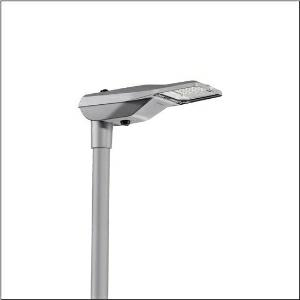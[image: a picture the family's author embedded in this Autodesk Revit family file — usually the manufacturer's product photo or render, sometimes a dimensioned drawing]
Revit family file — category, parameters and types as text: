
# Revit family: streetlight_sl_21_iq_micro___st1_0a_5xe1d31y08cb_1c09
name_source: partatom
category: Lighting Fixtures
units: mm (PartAtom-declared; Revit-internal decimal feet)

## family parameters
Cut with Voids When Loaded = No
Host = Face
Light Source = No
Part Type = Normal
Room Calculation Point = No
Round Connector Dimension = Use Diameter
Shared = No

## types (1)
- --- (1 x LED, 2880 lm, 19.1 W, 3000K)
    Apparent Load = 19 VA
    CIE Flux Codes = 37 72 97 100 100
    Color Rendering = 70
    Color Temperature = 3000K
    Default Elevation = 1800 mm
    Description = Streetlight SL 21 iQ micro, mast luminaire, primary light control with lens, of PMMA, primary optical cover: cover, of toughened safety glass, transparent, light distribution: ST1.0a, light emission: direct distribution, primary light characteristic: asymmetric, installation type: post-top, side-entry, LED, High Power LED, rated luminous flux: 2.880lm, luminous efficacy: 151lm/W, light colour: 730, colour temperature: 3000K, control gear: iQ-Street Remote, D4i with power reduction, control: pre-setting: logarithmic dimming characteristic, Street-Remote, Auto-Match, Temp-Guard, Lumen-Switch, Night-Set, Smart-Wire, Light-Fading, Desk-Remote (wireless, voltage-free reading and setting of iQ features in the workshop via application-optimized NFC function/RFID function), optimised constant luminous flux control (CLO 2.0), mains connection: 220..240V, AC, 50/60Hz, start of lifetime: 19W, end of service life: 20W, reduction: 9W, luminaire housing, of diecast aluminium, powder-coated, SITECO metallic grey (DB 702S), corrosivity category C5 high according to DIN EN ISO 12944, please order mast flange separately, inclination adjustable: 0°, 5°, 10°, 15°, sealing non-destructively replaceable, multi-level sealing system, length: 528mm, width: 235mm, height: 110mm, mast flange for spigot size: 42mm (side-entry): 5XC10008XM4, 60/48mm (side-entry/post-top): 5XC10108XM2, 76/60mm (side-entry/post-top): 5XC10108XM1, mounting height: 4..8m, Smart Interface below and above, protection rating (complete): IP66, insulation class (complete): insulation class II (safety insulation), certification: CE, ENEC, ENEC+, VDE, impact resistance: IK10, permissible operating ambient temperature for outdoor applications: -40..+50°C, standard-compliant lighting for roads and squares, packaging unit: 1 piece

Light Distribution: ST1.0a
    Height = 110 mm
    Lamp = 1 x LED
    Lamp Light Flux = 2880 lm
    Lamp Power = 19.1 W
    Lamp count = 1
    Length = 528 mm
    Luminous efficacy = 151 lm/W
    Manufacturer = Siteco
    ModVariant = No
    Model = 5XE1D31Y08CB
    Number of Poles = 1
    OnlyDefault = Yes
    Power Factor = 1
    Product Name = Streetlight SL 21 iQ micro | ST1.0a
    Product group = mast luminaire | pylon top
    ProductGroupID = 6100
    Protection Class = Protection class II
    Protection Degree = IP 66
    RLX_Detail_Level = 1
    RLX_Emergency_Light_Flux = 0 lm
    RLX_Emergency_Type = 0
    RLX_Emergency_Type_DB = No
    RlxData = <blob elided: 98429 chars, md5=2811ca85>
    Socket = socket
    Standby Power = 0 W
    System Light Flux = 2880 lm
    System Power = 19 W
    Type Comments = factory setting: luminous flux: 100 % | dim-lin: 254 | 387 mA
    Type Image = l_1007239.jpg
    URL = http://relux.com
    VarID = @adj_115579
    Voltage = 0 V
    Weight = 0.00 kg
    Width = 235 mm

## geometry (parser evidence)
native form markers: Blend x4, Sweep x11
no freeform markers — native parametric forms only
